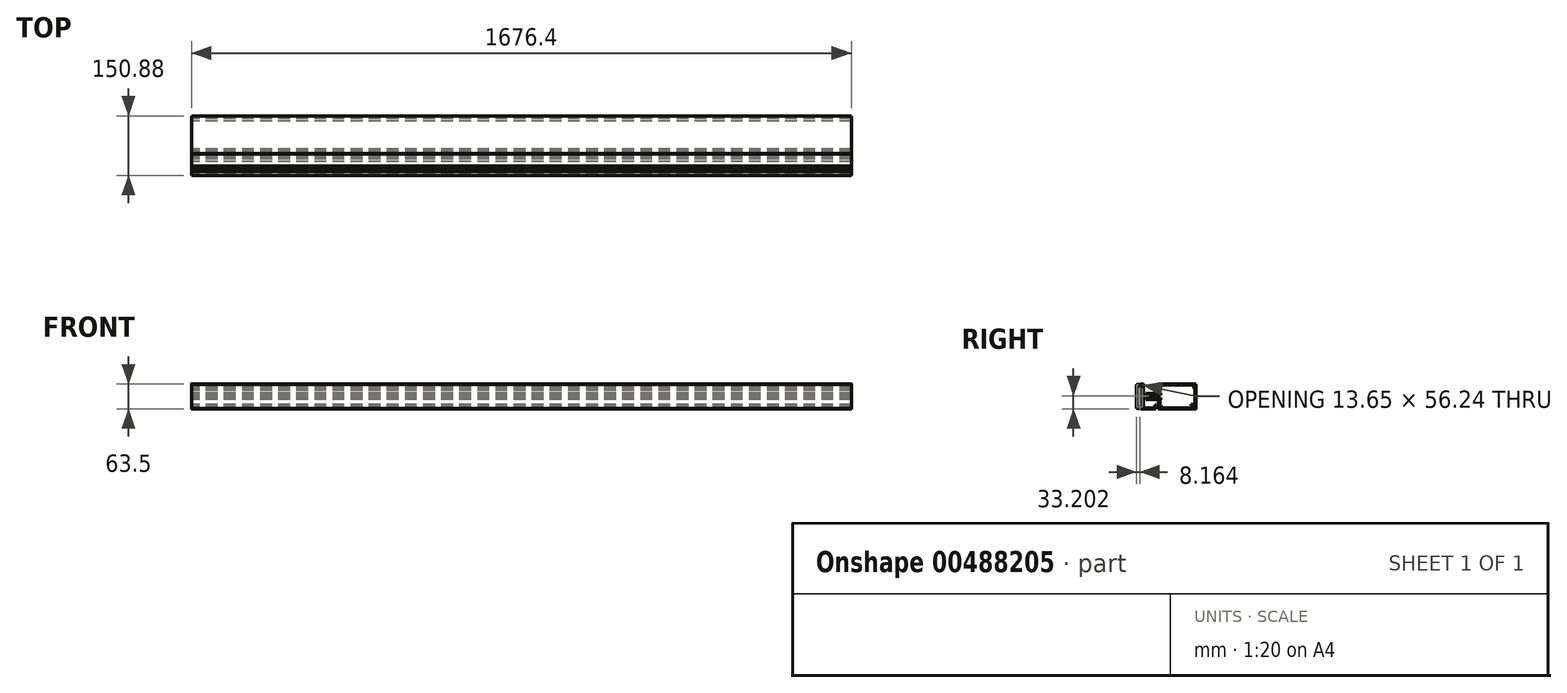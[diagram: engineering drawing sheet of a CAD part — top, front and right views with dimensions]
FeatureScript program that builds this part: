
annotation { "Feature Type Name" : "Feature", "Feature Type Description" : "" }
export const myFeature = defineFeature(function(context is Context, id is Id, definition is map)
    precondition{}
    {
        {
            var Q0;
            Q0=qCreatedBy(makeId("Right.planeOp"),FACE);
            var sketch = newSketch(context, id + "F0", { "sketchPlane" : qUnion([Q0])});
            skLineSegment(sketch, "E0", {"start": v(-82.55, 54.45) * mm, "end": v(-2.69, 54.45) * mm});
            skLineSegment(sketch, "E1", {"start": v(-2.69, 54.45) * mm, "end": v(-1.35, 59.85) * mm});
            skLineSegment(sketch, "E2", {"start": v(-1.35, 59.85) * mm, "end": v(1.35, 49.06) * mm});
            skLineSegment(sketch, "E3", {"start": v(1.35, 49.06) * mm, "end": v(2.69, 54.45) * mm});
            skLineSegment(sketch, "E4", {"start": v(2.69, 54.45) * mm, "end": v(82.55, 54.45) * mm});
            skLineSegment(sketch, "E5", {"start": v(-25.4, 54.45) * mm, "end": v(-25.4, -9.05) * mm});
            skLineSegment(sketch, "E6", {"start": v(-25.4, -9.05) * mm, "end": v(-50.8, -9.05) * mm});
            skLineSegment(sketch, "E7", {"start": v(-50.8, -9.05) * mm, "end": v(-50.8, 54.45) * mm});
            skLineSegment(sketch, "E8", {"start": v(-76.2, 3.65) * mm, "end": v(-76.2, 54.45) * mm});
            skLineSegment(sketch, "E9", {"start": v(-64.5, 4.75) * mm, "end": v(-64.5, 54.45) * mm});
            skLineSegment(sketch, "E10", {"start": v(-11.7, 4.75) * mm, "end": v(-11.7, 54.45) * mm});
            skLineSegment(sketch, "E11", {"start": v(-31.75, 54.45) * mm, "end": v(-31.75, -9.05) * mm});
            skLineSegment(sketch, "E12", {"start": v(-44.45, -9.05) * mm, "end": v(-44.45, 54.45) * mm});
            skLineSegment(sketch, "E13", {"start": v(-31.75, -2.7) * mm, "end": v(-44.45, -2.7) * mm});
            skLineSegment(sketch, "E14", {"start": v(76.2, 3.65) * mm, "end": v(76.2, 54.45) * mm});
            skArc(sketch, "E15", {"start": v(-18.4, -56.99) * mm, "mid": v(-17.66, -57.49) * mm, "end": v(-16.78, -57.66) * mm});
            skLineSegment(sketch, "E16", {"start": v(-16.78, -57.66) * mm, "end": v(-16.51, -57.66) * mm});
            skArc(sketch, "E17", {"start": v(-16.51, -57.66) * mm, "mid": v(-15.61, -57.29) * mm, "end": v(-15.24, -56.4) * mm});
            skLineSegment(sketch, "E18", {"start": v(-15.24, -56.4) * mm, "end": v(-15.24, -54.16) * mm});
            skArc(sketch, "E19", {"start": v(-15.24, -54.16) * mm, "mid": v(-15.61, -53.26) * mm, "end": v(-16.51, -52.89) * mm});
            skLineSegment(sketch, "E20", {"start": v(-16.51, -52.89) * mm, "end": v(-16.78, -52.89) * mm});
            skArc(sketch, "E21", {"start": v(-16.78, -52.89) * mm, "mid": v(-17.66, -53.06) * mm, "end": v(-18.4, -53.56) * mm});
            skArc(sketch, "E22", {"start": v(-19.05, -53.3) * mm, "mid": v(-18.81, -53.64) * mm, "end": v(-18.4, -53.56) * mm});
            skArc(sketch, "E23", {"start": v(-19.05, -34.78) * mm, "mid": v(-19.12, -34.6) * mm, "end": v(-19.3, -34.52) * mm});
            skLineSegment(sketch, "E24", {"start": v(-19.3, -34.52) * mm, "end": v(-20.73, -34.52) * mm});
            skArc(sketch, "E25", {"start": v(-20.73, -34.52) * mm, "mid": v(-20.9, -34.6) * mm, "end": v(-20.98, -34.78) * mm});
            skLineSegment(sketch, "E26", {"start": v(-20.98, -34.78) * mm, "end": v(-20.98, -35.8) * mm});
            skArc(sketch, "E27", {"start": v(-21.23, -36.05) * mm, "mid": v(-21.05, -35.97) * mm, "end": v(-20.98, -35.8) * mm});
            skLineSegment(sketch, "E28", {"start": v(-21.23, -36.05) * mm, "end": v(-50.8, -36.05) * mm});
            skLineSegment(sketch, "E29", {"start": v(-50.8, -36.05) * mm, "end": v(-50.8, -35.03) * mm});
            skLineSegment(sketch, "E30", {"start": v(-50.8, -35.03) * mm, "end": v(-51.18, -34.65) * mm});
            skLineSegment(sketch, "E31", {"start": v(-51.18, -34.65) * mm, "end": v(-50.8, -34.27) * mm});
            skLineSegment(sketch, "E32", {"start": v(-50.8, -34.27) * mm, "end": v(-50.8, -32.41) * mm});
            skLineSegment(sketch, "E33", {"start": v(-50.8, -32.41) * mm, "end": v(-51.18, -32.03) * mm});
            skLineSegment(sketch, "E34", {"start": v(-51.18, -32.03) * mm, "end": v(-50.8, -31.65) * mm});
            skLineSegment(sketch, "E35", {"start": v(-50.8, -31.65) * mm, "end": v(-50.8, -30.64) * mm});
            skLineSegment(sketch, "E36", {"start": v(-50.8, -30.64) * mm, "end": v(-39.88, -30.64) * mm});
            skLineSegment(sketch, "E37", {"start": v(-39.88, -30.64) * mm, "end": v(-34.34, -29.15) * mm});
            skArc(sketch, "E38", {"start": v(-34.34, -29.15) * mm, "mid": v(-33.53, -28.1) * mm, "end": v(-34.34, -27.04) * mm});
            skLineSegment(sketch, "E39", {"start": v(-34.34, -27.04) * mm, "end": v(-39.88, -25.56) * mm});
            skLineSegment(sketch, "E40", {"start": v(-39.88, -25.56) * mm, "end": v(-50.8, -25.56) * mm});
            skLineSegment(sketch, "E41", {"start": v(-50.8, -25.56) * mm, "end": v(-50.8, -24.54) * mm});
            skLineSegment(sketch, "E42", {"start": v(-50.8, -24.54) * mm, "end": v(-51.18, -24.16) * mm});
            skLineSegment(sketch, "E43", {"start": v(-51.18, -24.16) * mm, "end": v(-50.8, -23.78) * mm});
            skLineSegment(sketch, "E44", {"start": v(-50.8, -23.78) * mm, "end": v(-50.8, -21.92) * mm});
            skLineSegment(sketch, "E45", {"start": v(-50.8, -21.92) * mm, "end": v(-51.18, -21.54) * mm});
            skLineSegment(sketch, "E46", {"start": v(-51.18, -21.54) * mm, "end": v(-50.8, -21.16) * mm});
            skLineSegment(sketch, "E47", {"start": v(-50.8, -21.16) * mm, "end": v(-50.8, -20.15) * mm});
            skLineSegment(sketch, "E48", {"start": v(-50.8, -20.15) * mm, "end": v(-21.23, -20.15) * mm});
            skArc(sketch, "E49", {"start": v(-20.98, -20.4) * mm, "mid": v(-21.05, -20.22) * mm, "end": v(-21.23, -20.15) * mm});
            skLineSegment(sketch, "E50", {"start": v(-20.98, -20.4) * mm, "end": v(-20.98, -21.42) * mm});
            skArc(sketch, "E51", {"start": v(-20.98, -21.42) * mm, "mid": v(-20.9, -21.6) * mm, "end": v(-20.73, -21.67) * mm});
            skLineSegment(sketch, "E52", {"start": v(-20.73, -21.67) * mm, "end": v(-19.3, -21.67) * mm});
            skArc(sketch, "E53", {"start": v(-19.3, -21.67) * mm, "mid": v(-19.12, -21.6) * mm, "end": v(-19.05, -21.42) * mm});
            skLineSegment(sketch, "E54", {"start": v(-19.05, -21.42) * mm, "end": v(-19.05, -12.6) * mm});
            skLineSegment(sketch, "E55", {"start": v(-19.05, -12.6) * mm, "end": v(-18.67, -12.22) * mm});
            skLineSegment(sketch, "E56", {"start": v(-18.67, -12.22) * mm, "end": v(-19.05, -11.84) * mm});
            skLineSegment(sketch, "E57", {"start": v(-19.05, -11.84) * mm, "end": v(-19.05, -2.9) * mm});
            skArc(sketch, "E58", {"start": v(-18.4, -2.63) * mm, "mid": v(-18.81, -2.55) * mm, "end": v(-19.05, -2.9) * mm});
            skArc(sketch, "E59", {"start": v(-18.4, -2.63) * mm, "mid": v(-17.66, -3.13) * mm, "end": v(-16.78, -3.3) * mm});
            skLineSegment(sketch, "E60", {"start": v(-16.78, -3.3) * mm, "end": v(-16.51, -3.3) * mm});
            skArc(sketch, "E61", {"start": v(-16.51, -3.3) * mm, "mid": v(-15.61, -2.93) * mm, "end": v(-15.24, -2.04) * mm});
            skLineSegment(sketch, "E62", {"start": v(-15.24, -2.04) * mm, "end": v(-15.24, 0.2) * mm});
            skArc(sketch, "E63", {"start": v(-15.24, 0.2) * mm, "mid": v(-15.61, 1.1) * mm, "end": v(-16.51, 1.47) * mm});
            skLineSegment(sketch, "E64", {"start": v(-16.51, 1.47) * mm, "end": v(-16.78, 1.47) * mm});
            skArc(sketch, "E65", {"start": v(-16.78, 1.47) * mm, "mid": v(-17.66, 1.3) * mm, "end": v(-18.4, 0.8) * mm});
            skArc(sketch, "E66", {"start": v(-19.05, 1.06) * mm, "mid": v(-18.81, 0.71) * mm, "end": v(-18.4, 0.8) * mm});
            skLineSegment(sketch, "E67", {"start": v(-19.05, 1.06) * mm, "end": v(-19.05, 3.15) * mm});
            skArc(sketch, "E68", {"start": v(-18.54, 3.65) * mm, "mid": v(-18.9, 3.5) * mm, "end": v(-19.05, 3.15) * mm});
            skLineSegment(sketch, "E69", {"start": v(-18.54, 3.65) * mm, "end": v(76.2, 3.65) * mm});
            skLineSegment(sketch, "E70", {"start": v(76.2, 3.65) * mm, "end": v(76.2, -59.06) * mm});
            skArc(sketch, "E71", {"start": v(75.77, -59.24) * mm, "mid": v(76.04, -59.3) * mm, "end": v(76.2, -59.06) * mm});
            skLineSegment(sketch, "E72", {"start": v(75.77, -59.24) * mm, "end": v(72.37, -55.84) * mm});
            skLineSegment(sketch, "E73", {"start": v(72.37, -55.84) * mm, "end": v(70.94, -51.92) * mm});
            skLineSegment(sketch, "E74", {"start": v(70.94, -51.92) * mm, "end": v(72.26, -51.92) * mm});
            skArc(sketch, "E75", {"start": v(72.26, -51.92) * mm, "mid": v(72.8, -51.7) * mm, "end": v(73.02, -51.16) * mm});
            skLineSegment(sketch, "E76", {"start": v(73.03, -51.16) * mm, "end": v(73.03, -9.17) * mm});
            skArc(sketch, "E77", {"start": v(73.02, -9.17) * mm, "mid": v(72.58, -8.1) * mm, "end": v(71.5, -7.65) * mm});
            skLineSegment(sketch, "E78", {"start": v(71.5, -7.65) * mm, "end": v(70.61, -7.65) * mm});
            skLineSegment(sketch, "E79", {"start": v(70.61, -7.65) * mm, "end": v(70.61, -4.47) * mm});
            skLineSegment(sketch, "E80", {"start": v(70.61, -4.47) * mm, "end": v(71.5, -4.47) * mm});
            skArc(sketch, "E81", {"start": v(71.5, -4.47) * mm, "mid": v(72.58, -4.03) * mm, "end": v(73.02, -2.95) * mm});
            skLineSegment(sketch, "E82", {"start": v(73.03, -2.95) * mm, "end": v(73.03, 0.35) * mm});
            skArc(sketch, "E83", {"start": v(73.02, 0.35) * mm, "mid": v(72.8, 0.9) * mm, "end": v(72.26, 1.11) * mm});
            skLineSegment(sketch, "E84", {"start": v(72.26, 1.11) * mm, "end": v(-11.94, 1.11) * mm});
            skArc(sketch, "E85", {"start": v(-11.94, 1.11) * mm, "mid": v(-12.48, 0.9) * mm, "end": v(-12.7, 0.35) * mm});
            skLineSegment(sketch, "E86", {"start": v(-12.7, 0.35) * mm, "end": v(-12.7, -4.85) * mm});
            skLineSegment(sketch, "E87", {"start": v(-13.2, -5.36) * mm, "end": v(-15.88, -5.36) * mm});
            skLineSegment(sketch, "E88", {"start": v(-15.88, -5.36) * mm, "end": v(-15.88, -20.15) * mm});
            skLineSegment(sketch, "E89", {"start": v(-15.88, -20.15) * mm, "end": v(-13.46, -20.15) * mm});
            skArc(sketch, "E90", {"start": v(-12.7, -20.9) * mm, "mid": v(-12.92, -20.37) * mm, "end": v(-13.46, -20.15) * mm});
            skLineSegment(sketch, "E91", {"start": v(-12.7, -20.9) * mm, "end": v(-12.7, -22.56) * mm});
            skArc(sketch, "E92", {"start": v(-13.46, -23.32) * mm, "mid": v(-12.92, -23.1) * mm, "end": v(-12.7, -22.56) * mm});
            skLineSegment(sketch, "E93", {"start": v(-13.46, -23.32) * mm, "end": v(-15.88, -23.32) * mm});
            skArc(sketch, "E94", {"start": v(-17.4, -24.84) * mm, "mid": v(-16.32, -24.4) * mm, "end": v(-15.88, -23.32) * mm});
            skLineSegment(sketch, "E95", {"start": v(-17.4, -24.84) * mm, "end": v(-22.63, -24.84) * mm});
            skArc(sketch, "E96", {"start": v(-24.16, -23.32) * mm, "mid": v(-23.7, -24.4) * mm, "end": v(-22.63, -24.84) * mm});
            skLineSegment(sketch, "E97", {"start": v(-24.16, -23.32) * mm, "end": v(-32.48, -23.32) * mm});
            skArc(sketch, "E98", {"start": v(-32.48, -23.32) * mm, "mid": v(-32.97, -23.71) * mm, "end": v(-32.7, -24.28) * mm});
            skArc(sketch, "E99", {"start": v(-32.7, -31.9) * mm, "mid": v(-30.35, -28.1) * mm, "end": v(-32.7, -24.28) * mm});
            skArc(sketch, "E100", {"start": v(-32.7, -31.9) * mm, "mid": v(-32.97, -32.48) * mm, "end": v(-32.48, -32.87) * mm});
            skLineSegment(sketch, "E101", {"start": v(-32.48, -32.87) * mm, "end": v(-24.16, -32.87) * mm});
            skArc(sketch, "E102", {"start": v(-22.63, -31.35) * mm, "mid": v(-23.7, -31.8) * mm, "end": v(-24.16, -32.87) * mm});
            skLineSegment(sketch, "E103", {"start": v(-22.63, -31.35) * mm, "end": v(-17.4, -31.35) * mm});
            skArc(sketch, "E104", {"start": v(-15.88, -32.87) * mm, "mid": v(-16.32, -31.8) * mm, "end": v(-17.4, -31.35) * mm});
            skLineSegment(sketch, "E105", {"start": v(-15.88, -32.87) * mm, "end": v(-13.46, -32.87) * mm});
            skArc(sketch, "E106", {"start": v(-12.7, -33.63) * mm, "mid": v(-12.92, -33.1) * mm, "end": v(-13.46, -32.87) * mm});
            skLineSegment(sketch, "E107", {"start": v(-12.7, -33.63) * mm, "end": v(-12.7, -35.28) * mm});
            skArc(sketch, "E108", {"start": v(-13.46, -36.05) * mm, "mid": v(-12.92, -35.82) * mm, "end": v(-12.7, -35.28) * mm});
            skLineSegment(sketch, "E109", {"start": v(-13.46, -36.05) * mm, "end": v(-15.88, -36.05) * mm});
            skLineSegment(sketch, "E110", {"start": v(-15.88, -36.05) * mm, "end": v(-15.88, -50.83) * mm});
            skLineSegment(sketch, "E111", {"start": v(-15.88, -50.83) * mm, "end": v(-13.2, -50.83) * mm});
            skArc(sketch, "E112", {"start": v(-12.7, -51.34) * mm, "mid": v(-12.85, -50.98) * mm, "end": v(-13.2, -50.83) * mm});
            skLineSegment(sketch, "E113", {"start": v(-12.7, -51.34) * mm, "end": v(-12.7, -56.54) * mm});
            skLineSegment(sketch, "E114", {"start": v(-12.7, -56.54) * mm, "end": v(-10.64, -56.54) * mm});
            skArc(sketch, "E115", {"start": v(-10.64, -58.07) * mm, "mid": v(-9.88, -57.3) * mm, "end": v(-10.64, -56.54) * mm});
            skLineSegment(sketch, "E116", {"start": v(-10.64, -58.07) * mm, "end": v(-12.7, -58.07) * mm});
            skLineSegment(sketch, "E117", {"start": v(-12.7, -58.07) * mm, "end": v(-12.7, -59.34) * mm});
            skArc(sketch, "E118", {"start": v(-13.2, -59.85) * mm, "mid": v(-12.85, -59.7) * mm, "end": v(-12.7, -59.34) * mm});
            skLineSegment(sketch, "E119", {"start": v(-13.2, -59.85) * mm, "end": v(-18.54, -59.85) * mm});
            skArc(sketch, "E120", {"start": v(-19.05, -59.34) * mm, "mid": v(-18.9, -59.7) * mm, "end": v(-18.54, -59.85) * mm});
            skLineSegment(sketch, "E121", {"start": v(-19.05, -59.34) * mm, "end": v(-19.05, -57.25) * mm});
            skArc(sketch, "E122", {"start": v(-18.4, -56.99) * mm, "mid": v(-18.81, -56.9) * mm, "end": v(-19.05, -57.25) * mm});
            skLineSegment(sketch, "E123", {"start": v(-50.8, -36.05) * mm, "end": v(-50.8, -34.46) * mm});
            skLineSegment(sketch, "E124", {"start": v(-57.15, -36.05) * mm, "end": v(-50.8, -36.05) * mm});
            skLineSegment(sketch, "E125", {"start": v(-50.8, -20.15) * mm, "end": v(-57.15, -20.15) * mm});
            skLineSegment(sketch, "E126", {"start": v(-50.8, -21.73) * mm, "end": v(-50.8, -20.15) * mm});
            skLineSegment(sketch, "E127", {"start": v(-57.15, -36.05) * mm, "end": v(-57.15, -34.46) * mm});
            skLineSegment(sketch, "E128", {"start": v(-57.15, -21.73) * mm, "end": v(-57.15, -20.15) * mm});
            skLineSegment(sketch, "E129", {"start": v(-31.75, -16.97) * mm, "end": v(-41.28, -16.97) * mm});
            skLineSegment(sketch, "E130", {"start": v(-41.28, -16.97) * mm, "end": v(-41.28, -20.15) * mm});
            skLineSegment(sketch, "E131", {"start": v(-41.28, -20.15) * mm, "end": v(-50.8, -20.15) * mm});
            skLineSegment(sketch, "E132", {"start": v(-50.8, -20.15) * mm, "end": v(-50.8, -12.22) * mm});
            skLineSegment(sketch, "E133", {"start": v(-50.8, -12.22) * mm, "end": v(-52.39, -12.22) * mm});
            skArc(sketch, "E134", {"start": v(-52.39, -9.05) * mm, "mid": v(-53.98, -10.63) * mm, "end": v(-52.39, -12.22) * mm});
            skLineSegment(sketch, "E135", {"start": v(-52.39, -9.05) * mm, "end": v(-20.64, -9.05) * mm});
            skArc(sketch, "E136", {"start": v(-20.64, -12.22) * mm, "mid": v(-19.05, -10.63) * mm, "end": v(-20.64, -9.05) * mm});
            skLineSegment(sketch, "E137", {"start": v(-20.64, -12.22) * mm, "end": v(-22.23, -12.22) * mm});
            skLineSegment(sketch, "E138", {"start": v(-22.23, -12.22) * mm, "end": v(-22.23, -20.15) * mm});
            skLineSegment(sketch, "E139", {"start": v(-22.23, -20.15) * mm, "end": v(-31.75, -20.15) * mm});
            skLineSegment(sketch, "E140", {"start": v(-31.75, -20.15) * mm, "end": v(-31.75, -16.97) * mm});
            skLineSegment(sketch, "E141", {"start": v(-19.06, -8.53) * mm, "end": v(-25.4, -8.53) * mm});
            skLineSegment(sketch, "E142", {"start": v(-25.4, 7.13) * mm, "end": v(-11.7, 5.19) * mm});
            skLineSegment(sketch, "E143", {"start": v(-11.7, 5.19) * mm, "end": v(-11.7, 3.66) * mm});
            skLineSegment(sketch, "E144", {"start": v(-11.7, 3.66) * mm, "end": v(-14.63, 3.66) * mm});
            skLineSegment(sketch, "E145", {"start": v(-57.14, -8.53) * mm, "end": v(-50.8, -8.53) * mm});
            skLineSegment(sketch, "E146", {"start": v(-50.8, 7.13) * mm, "end": v(-64.5, 5.19) * mm});
            skLineSegment(sketch, "E147", {"start": v(-64.5, 5.19) * mm, "end": v(-64.5, 3.66) * mm});
            skLineSegment(sketch, "E148", {"start": v(-64.5, 3.66) * mm, "end": v(-61.57, 3.66) * mm});
            skLineSegment(sketch, "E149", {"start": v(-57.15, -24.72) * mm, "end": v(-60.33, -24.72) * mm});
            skLineSegment(sketch, "E150", {"start": v(-57.15, -31.47) * mm, "end": v(-60.33, -31.47) * mm});
            skLineSegment(sketch, "E151", {"start": v(-74.68, -58.58) * mm, "end": v(-65.43, -58.58) * mm});
            skLineSegment(sketch, "E152", {"start": v(-65.43, -58.58) * mm, "end": v(-65.43, -57.81) * mm});
            skArc(sketch, "E153", {"start": v(-63.4, -57.81) * mm, "mid": v(-64.41, -56.8) * mm, "end": v(-65.43, -57.81) * mm});
            skLineSegment(sketch, "E154", {"start": v(-63.4, -57.81) * mm, "end": v(-63.4, -58.32) * mm});
            skArc(sketch, "E155", {"start": v(-64.92, -59.85) * mm, "mid": v(-63.84, -59.4) * mm, "end": v(-63.4, -58.32) * mm});
            skLineSegment(sketch, "E156", {"start": v(-64.92, -59.85) * mm, "end": v(-76.2, -59.85) * mm});
            skLineSegment(sketch, "E157", {"start": v(-76.2, 3.65) * mm, "end": v(-64.92, 3.65) * mm});
            skArc(sketch, "E158", {"start": v(-63.4, 2.13) * mm, "mid": v(-63.84, 3.2) * mm, "end": v(-64.92, 3.65) * mm});
            skLineSegment(sketch, "E159", {"start": v(-63.4, 2.13) * mm, "end": v(-63.4, 1.62) * mm});
            skArc(sketch, "E160", {"start": v(-65.43, 1.62) * mm, "mid": v(-64.41, 0.6) * mm, "end": v(-63.4, 1.62) * mm});
            skLineSegment(sketch, "E161", {"start": v(-65.43, 1.62) * mm, "end": v(-65.43, 2.38) * mm});
            skLineSegment(sketch, "E162", {"start": v(-65.43, 2.38) * mm, "end": v(-74.68, 2.38) * mm});
            skLineSegment(sketch, "E163", {"start": v(-74.68, 2.38) * mm, "end": v(-74.68, -58.58) * mm});
            skLineSegment(sketch, "E164", {"start": v(-59.7, -5.85) * mm, "end": v(-59.7, -19.84) * mm});
            skLineSegment(sketch, "E165", {"start": v(-59.7, -19.84) * mm, "end": v(-60.33, -20.48) * mm});
            skLineSegment(sketch, "E166", {"start": v(-60.33, -20.48) * mm, "end": v(-60.33, -27.71) * mm});
            skLineSegment(sketch, "E167", {"start": v(-60.33, -28.48) * mm, "end": v(-60.33, -35.72) * mm});
            skLineSegment(sketch, "E168", {"start": v(-60.33, -35.72) * mm, "end": v(-59.7, -36.35) * mm});
            skLineSegment(sketch, "E169", {"start": v(-59.7, -36.35) * mm, "end": v(-59.7, -54.77) * mm});
            skLineSegment(sketch, "E170", {"start": v(-59.7, -54.77) * mm, "end": v(-66.57, -54.77) * mm});
            skArc(sketch, "E171", {"start": v(-63.14, -58.07) * mm, "mid": v(-64.2, -56.81) * mm, "end": v(-65.62, -57.66) * mm});
            skLineSegment(sketch, "E172", {"start": v(-63.14, -58.07) * mm, "end": v(-63.14, -59.08) * mm});
            skArc(sketch, "E173", {"start": v(-63.14, -59.08) * mm, "mid": v(-62.92, -59.62) * mm, "end": v(-62.38, -59.85) * mm});
            skLineSegment(sketch, "E174", {"start": v(-62.38, -59.85) * mm, "end": v(-25.4, -59.85) * mm});
            skLineSegment(sketch, "E175", {"start": v(-25.4, -59.85) * mm, "end": v(-25.4, -50.45) * mm});
            skArc(sketch, "E176", {"start": v(-25.4, -50.45) * mm, "mid": v(-25.62, -49.9) * mm, "end": v(-26.16, -49.69) * mm});
            skLineSegment(sketch, "E177", {"start": v(-26.16, -49.69) * mm, "end": v(-27.18, -49.69) * mm});
            skArc(sketch, "E178", {"start": v(-27.18, -49.69) * mm, "mid": v(-27.72, -49.9) * mm, "end": v(-27.94, -50.45) * mm});
            skLineSegment(sketch, "E179", {"start": v(-27.94, -50.45) * mm, "end": v(-27.94, -55.78) * mm});
            skArc(sketch, "E180", {"start": v(-29.46, -57.3) * mm, "mid": v(-28.39, -56.86) * mm, "end": v(-27.94, -55.78) * mm});
            skLineSegment(sketch, "E181", {"start": v(-29.46, -57.3) * mm, "end": v(-55.63, -57.3) * mm});
            skArc(sketch, "E182", {"start": v(-57.15, -55.78) * mm, "mid": v(-56.7, -56.86) * mm, "end": v(-55.63, -57.3) * mm});
            skLineSegment(sketch, "E183", {"start": v(-57.15, -55.78) * mm, "end": v(-57.15, -33.81) * mm});
            skLineSegment(sketch, "E184", {"start": v(-57.15, -33.81) * mm, "end": v(-56.77, -33.43) * mm});
            skLineSegment(sketch, "E185", {"start": v(-56.77, -33.43) * mm, "end": v(-57.15, -33.05) * mm});
            skLineSegment(sketch, "E186", {"start": v(-57.15, -33.05) * mm, "end": v(-57.15, -23.14) * mm});
            skLineSegment(sketch, "E187", {"start": v(-57.15, -23.14) * mm, "end": v(-56.77, -22.76) * mm});
            skLineSegment(sketch, "E188", {"start": v(-56.77, -22.76) * mm, "end": v(-57.15, -22.38) * mm});
            skLineSegment(sketch, "E189", {"start": v(-57.15, -22.38) * mm, "end": v(-57.15, -2.9) * mm});
            skArc(sketch, "E190", {"start": v(-57.15, -2.9) * mm, "mid": v(-57.39, -2.55) * mm, "end": v(-57.8, -2.63) * mm});
            skArc(sketch, "E191", {"start": v(-59.42, -3.3) * mm, "mid": v(-58.54, -3.13) * mm, "end": v(-57.8, -2.63) * mm});
            skLineSegment(sketch, "E192", {"start": v(-59.42, -3.3) * mm, "end": v(-59.7, -3.3) * mm});
            skArc(sketch, "E193", {"start": v(-60.96, -2.04) * mm, "mid": v(-60.59, -2.93) * mm, "end": v(-59.7, -3.3) * mm});
            skLineSegment(sketch, "E194", {"start": v(-60.96, -2.04) * mm, "end": v(-60.96, 0.2) * mm});
            skArc(sketch, "E195", {"start": v(-59.7, 1.47) * mm, "mid": v(-60.59, 1.1) * mm, "end": v(-60.96, 0.2) * mm});
            skLineSegment(sketch, "E196", {"start": v(-59.7, 1.47) * mm, "end": v(-59.42, 1.47) * mm});
            skArc(sketch, "E197", {"start": v(-57.8, 0.8) * mm, "mid": v(-58.54, 1.3) * mm, "end": v(-59.42, 1.47) * mm});
            skArc(sketch, "E198", {"start": v(-57.8, 0.8) * mm, "mid": v(-57.39, 0.71) * mm, "end": v(-57.15, 1.06) * mm});
            skLineSegment(sketch, "E199", {"start": v(-57.15, 1.06) * mm, "end": v(-57.15, 3.15) * mm});
            skArc(sketch, "E200", {"start": v(-57.15, 3.15) * mm, "mid": v(-57.3, 3.5) * mm, "end": v(-57.66, 3.65) * mm});
            skLineSegment(sketch, "E201", {"start": v(-57.66, 3.65) * mm, "end": v(-62.38, 3.65) * mm});
            skArc(sketch, "E202", {"start": v(-62.38, 3.65) * mm, "mid": v(-62.92, 3.43) * mm, "end": v(-63.14, 2.9) * mm});
            skLineSegment(sketch, "E203", {"start": v(-63.14, 2.9) * mm, "end": v(-63.14, 1.88) * mm});
            skArc(sketch, "E204", {"start": v(-65.62, 1.47) * mm, "mid": v(-64.2, 0.62) * mm, "end": v(-63.14, 1.88) * mm});
            skLineSegment(sketch, "E205", {"start": v(-65.62, 1.47) * mm, "end": v(-70.26, -1.2) * mm});
            skArc(sketch, "E206", {"start": v(-70.26, -1.2) * mm, "mid": v(-70.63, -2.6) * mm, "end": v(-69.24, -2.97) * mm});
            skLineSegment(sketch, "E207", {"start": v(-69.24, -2.97) * mm, "end": v(-66.57, -1.43) * mm});
            skLineSegment(sketch, "E208", {"start": v(-66.57, -1.43) * mm, "end": v(-63.14, -1.43) * mm});
            skLineSegment(sketch, "E209", {"start": v(-63.14, -1.43) * mm, "end": v(-63.14, -4.32) * mm});
            skArc(sketch, "E210", {"start": v(-63.14, -4.32) * mm, "mid": v(-62.7, -5.4) * mm, "end": v(-61.62, -5.85) * mm});
            skLineSegment(sketch, "E211", {"start": v(-61.62, -5.85) * mm, "end": v(-59.7, -5.85) * mm});
            skLineSegment(sketch, "E212", {"start": v(73.48, -57.3) * mm, "end": v(70.94, -57.3) * mm});
            skLineSegment(sketch, "E213", {"start": v(70.94, -57.3) * mm, "end": v(70.94, -51.92) * mm});
            skLineSegment(sketch, "E214", {"start": v(70.94, -51.92) * mm, "end": v(71.75, -51.92) * mm});
            skLineSegment(sketch, "E215", {"start": v(71.75, -51.92) * mm, "end": v(70.08, -49.01) * mm});
            skArc(sketch, "E216", {"start": v(70.08, -49.01) * mm, "mid": v(69.94, -48.87) * mm, "end": v(69.75, -48.82) * mm});
            skLineSegment(sketch, "E217", {"start": v(69.75, -48.82) * mm, "end": v(63.02, -48.82) * mm});
            skLineSegment(sketch, "E218", {"start": v(63.02, -48.82) * mm, "end": v(63.02, -50.4) * mm});
            skLineSegment(sketch, "E219", {"start": v(63.02, -50.4) * mm, "end": v(69.37, -50.4) * mm});
            skLineSegment(sketch, "E220", {"start": v(69.37, -50.4) * mm, "end": v(69.37, -57.56) * mm});
            skLineSegment(sketch, "E221", {"start": v(69.37, -57.56) * mm, "end": v(-8.23, -57.56) * mm});
            skLineSegment(sketch, "E222", {"start": v(-8.23, -57.56) * mm, "end": v(-8.23, -56.29) * mm});
            skArc(sketch, "E223", {"start": v(-8.23, -56.29) * mm, "mid": v(-8.68, -55.21) * mm, "end": v(-9.75, -54.77) * mm});
            skLineSegment(sketch, "E224", {"start": v(-9.75, -54.77) * mm, "end": v(-11.79, -54.77) * mm});
            skArc(sketch, "E225", {"start": v(-11.79, -54.77) * mm, "mid": v(-12.55, -55.53) * mm, "end": v(-11.79, -56.29) * mm});
            skLineSegment(sketch, "E226", {"start": v(-11.79, -56.29) * mm, "end": v(-9.88, -56.29) * mm});
            skLineSegment(sketch, "E227", {"start": v(-9.82, -56.3) * mm, "end": v(-9.84, -58.32) * mm});
            skLineSegment(sketch, "E228", {"start": v(-9.88, -58.32) * mm, "end": v(-12.04, -58.32) * mm});
            skArc(sketch, "E229", {"start": v(-12.04, -58.32) * mm, "mid": v(-12.4, -58.47) * mm, "end": v(-12.55, -58.83) * mm});
            skLineSegment(sketch, "E230", {"start": v(-12.55, -58.83) * mm, "end": v(-12.55, -59.85) * mm});
            skLineSegment(sketch, "E231", {"start": v(-12.55, -59.85) * mm, "end": v(75.41, -59.85) * mm});
            skArc(sketch, "E232", {"start": v(75.41, -59.85) * mm, "mid": v(75.65, -59.69) * mm, "end": v(75.6, -59.41) * mm});
            skLineSegment(sketch, "E233", {"start": v(75.6, -59.41) * mm, "end": v(73.48, -57.3) * mm});
            skLineSegment(sketch, "E234", {"start": v(75.72, -59.85) * mm, "end": v(76.2, -59.85) * mm});
            skLineSegment(sketch, "E235", {"start": v(76.2, -59.85) * mm, "end": v(76.2, -59.36) * mm});
            skLineSegment(sketch, "E236", {"start": v(-25.4, -59.85) * mm, "end": v(-18.54, -59.85) * mm});
            skLineSegment(sketch, "E237", {"start": v(-12.7, -4.85) * mm, "end": v(-13.2, -5.36) * mm});
            skLineSegment(sketch, "E238", {"start": v(-60.33, -28.48) * mm, "end": v(-60.33, -27.71) * mm});
            skLineSegment(sketch, "E239", {"start": v(-66.57, -54.77) * mm, "end": v(-73.34, -54.77) * mm});
            skLineSegment(sketch, "E240", {"start": v(-73.34, -54.77) * mm, "end": v(-73.34, -1.01) * mm});
            skLineSegment(sketch, "E241", {"start": v(-73.34, -1.01) * mm, "end": v(-65.62, 1.47) * mm});
            skLineSegment(sketch, "E242", {"start": v(-19.05, -53.3) * mm, "end": v(-19.05, -34.78) * mm});
            skLineSegment(sketch, "E243", {"start": v(-9.88, -56.29) * mm, "end": v(-9.82, -56.3) * mm});
            skLineSegment(sketch, "E244", {"start": v(-9.88, -58.32) * mm, "end": v(-9.84, -58.32) * mm});
            skLineSegment(sketch, "E245", {"start": v(-50.8, -25.56) * mm, "end": v(-50.8, -30.64) * mm});
            skSolve(sketch);
        }
        {
            var Q0;
            Q0=makeQuery(id+"F0.imprint","IMPRINT",FACE,{"disambiguationData":[TD([[makeQuery(id+"F0.imprint","IMPRINT",EDGE,{"derivedFrom":sQuery(id+"F0.wireOp",EDGE,"E212")}),1.0]])]});
            var Q1;
            {var subQ6=sQuery(id+"F0.wireOp",EDGE,"E150");Q1=makeQuery(id+"F0.imprint","IMPRINT",FACE,{"disambiguationData":[TD([[makeQuery(id+"F0.imprint","IMPRINT",EDGE,{"derivedFrom":subQ6}),1.0]])]});}
            var Q2;
            {var subQ1=sQuery(id+"F0.wireOp",EDGE,"E149");Q2=makeQuery(id+"F0.imprint","IMPRINT",FACE,{"disambiguationData":[TD([[makeQuery(id+"F0.imprint","IMPRINT",EDGE,{"derivedFrom":subQ1}),-1.0]])]});}
            var Q3;
            Q3=makeQuery(id+"F0.imprint","IMPRINT",FACE,{"disambiguationData":[TD([[makeQuery(id+"F0.imprint","IMPRINT",EDGE,{"derivedFrom":sQuery(id+"F0.wireOp",EDGE,"E15")}),-1.0]])]});
            extrude(context, id + "F1", {"entities" : qUnion([Q0, Q1, Q2, Q3]), "depth" : 1676.4 * mm});
        }
        {
            var Q0;
            {var subQ4=sQuery(id+"F0.wireOp",EDGE,"E149");Q0=makeQuery(id+"F0.imprint","IMPRINT",FACE,{"disambiguationData":[TD([[makeQuery(id+"F0.imprint","IMPRINT",EDGE,{"derivedFrom":subQ4}),1.0]])]});}
            extrude(context, id + "F2", {"entities" : qUnion([Q0]), "operationType" : NewBodyOperationType.ADD, "depth" : 1676.4 * mm, "offsetDistance" : 25.4 * mm});
        }
    });
